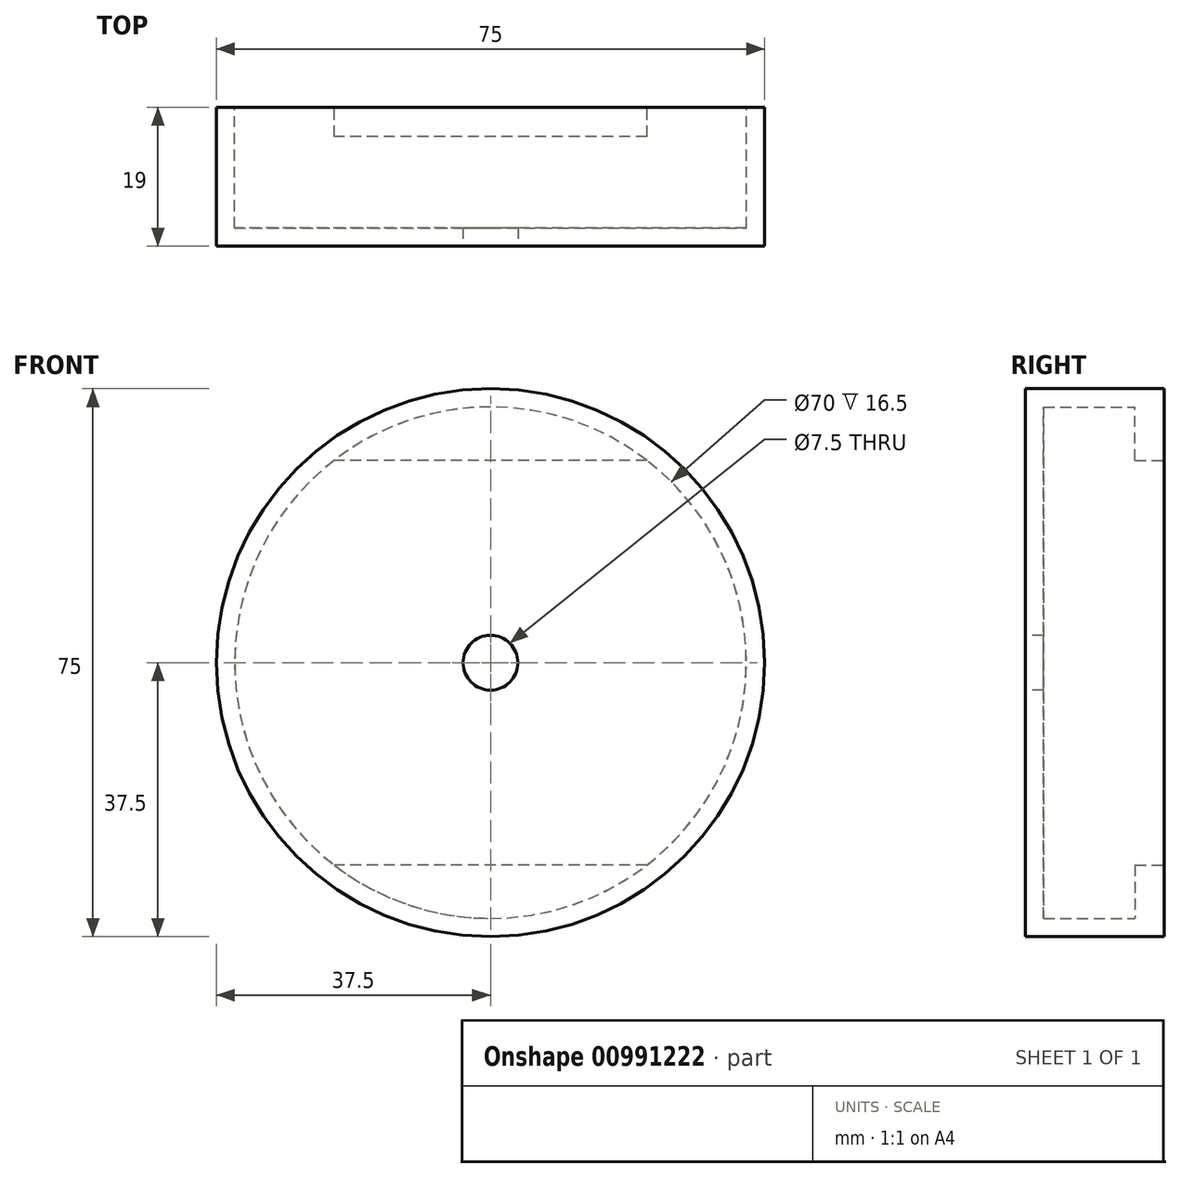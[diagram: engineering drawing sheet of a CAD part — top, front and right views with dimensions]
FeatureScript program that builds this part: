
annotation { "Feature Type Name" : "Feature", "Feature Type Description" : "" }
export const myFeature = defineFeature(function(context is Context, id is Id, definition is map)
    precondition{}
    {
        {
            var Q0;
            Q0=qCreatedBy(makeId("Front.planeOp"),FACE);
            var sketch = newSketch(context, id + "F0", { "sketchPlane" : qUnion([Q0])});
            skCircle(sketch, "E0", {"center": v(0, 0) * mm, "radius": 37.5 * mm});
            skSolve(sketch);
        }
        {
            var Q0;
            Q0 = qSketchRegion(id + "F0", true);
            extrude(context, id + "F1", {"entities" : qUnion([Q0]), "depth" : 19 * mm, "offsetDistance" : 25 * mm});
        }
        {
            var Q0;
            Q0=makeQuery(id+"F1.opExtrude","CAP_FACE",FACE,{"disambiguationData":[OSD([sQuery(id+"F0.wireOp",EDGE,"E0")])],"isStart":true});
            shell(context, id + "F2", {"entities" : qUnion([Q0]), "thickness" : 2.5 * mm});
        }
        {
            var Q0;
            Q0=makeQuery(id+"F1.opExtrude","CAP_FACE",FACE,{"disambiguationData":[OSD([sQuery(id+"F0.wireOp",EDGE,"E0")])],"isStart":false});
            var sketch = newSketch(context, id + "F3", { "sketchPlane" : qUnion([Q0])});
            skCircle(sketch, "E1", {"center": v(0, 0) * mm, "radius": 3.75 * mm});
            skSolve(sketch);
        }
        {
            var Q0;
            Q0 = qSketchRegion(id + "F3", true);
            extrude(context, id + "F4", {"entities" : qUnion([Q0]), "operationType" : NewBodyOperationType.REMOVE, "endBound" : BoundingType.THROUGH_ALL, "oppositeDirection" : true, "depth" : 25 * mm, "offsetDistance" : 25 * mm});
        }
        {
            var Q0;
            Q0=makeQuery(id+"F1.opExtrude","CAP_FACE",FACE,{"disambiguationData":[OSD([sQuery(id+"F0.wireOp",EDGE,"E0")])],"isStart":true});
            var sketch = newSketch(context, id + "F5", { "sketchPlane" : qUnion([Q0])});
            skLineSegment(sketch, "E2", {"start": v(-21.4, 27.7) * mm, "end": v(21.4, 27.7) * mm});
            skSolve(sketch);
        }
        {
            var Q0;
            {var subQ0=sQuery(id+"F5.wireOp",EDGE,"E2");Q0=makeQuery(id+"F5.imprint","IMPRINT",FACE,{"disambiguationData":[TD([[makeQuery(id+"F5.imprint","IMPRINT",EDGE,{"derivedFrom":subQ0}),1.0]])]});}
            extrude(context, id + "F6", {"entities" : qUnion([Q0]), "operationType" : NewBodyOperationType.ADD, "oppositeDirection" : true, "depth" : 4 * mm, "offsetDistance" : 25 * mm});
        }
        {
            var Q0;
            {var subQ0=sQuery(id+"F0.wireOp",EDGE,"E0");Q0=makeQuery(id+"F6.boolean.opBoolean","MERGE",FACE,{"derivedFrom":[makeQuery(id+"F1.opExtrude","CAP_FACE",FACE,{"disambiguationData":[OSD([subQ0])],"isStart":true}),makeQuery(id+"F6.opExtrude","CAP_FACE",FACE,{"disambiguationData":[OSD([subQ0,sQuery(id+"F5.wireOp",EDGE,"E2")])],"isStart":true})]});}
            var sketch = newSketch(context, id + "F7", { "sketchPlane" : qUnion([Q0])});
            skLineSegment(sketch, "E3", {"start": v(-21.4, -27.7) * mm, "end": v(21.4, -27.7) * mm});
            skSolve(sketch);
        }
        {
            var Q0;
            {var subQ0=sQuery(id+"F7.wireOp",EDGE,"E3");Q0=makeQuery(id+"F7.imprint","IMPRINT",FACE,{"disambiguationData":[TD([[makeQuery(id+"F7.imprint","IMPRINT",EDGE,{"derivedFrom":subQ0}),-1.0]])]});}
            extrude(context, id + "F8", {"entities" : qUnion([Q0]), "operationType" : NewBodyOperationType.ADD, "oppositeDirection" : true, "depth" : 4 * mm, "offsetDistance" : 25 * mm});
        }
    });
